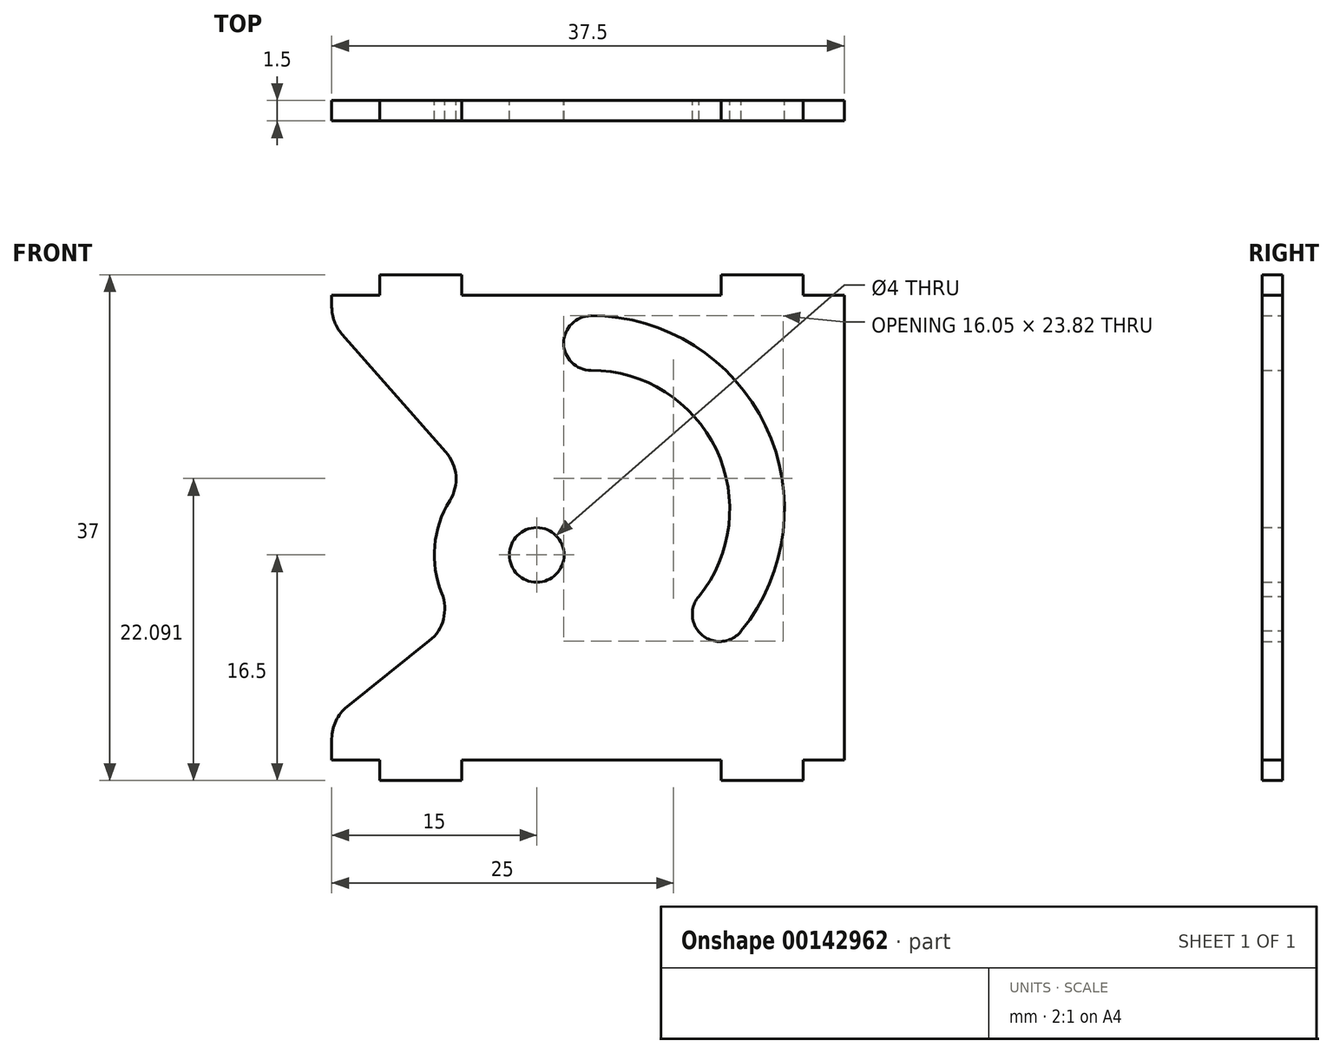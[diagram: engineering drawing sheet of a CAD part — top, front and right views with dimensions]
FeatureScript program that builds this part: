
annotation { "Feature Type Name" : "Feature", "Feature Type Description" : "" }
export const myFeature = defineFeature(function(context is Context, id is Id, definition is map)
    precondition{}
    {
        {
            var Q0;
            Q0=qCreatedBy(makeId("Front.planeOp"),FACE);
            var sketch = newSketch(context, id + "F0", { "sketchPlane" : qUnion([Q0])});
            skLineSegment(sketch, "E0.bottom", {"start": v(15, -19) * mm, "end": v(9, -19) * mm});
            skLineSegment(sketch, "E0.top", {"start": v(15, 18) * mm, "end": v(9, 18) * mm});
            skLineSegment(sketch, "E0.right", {"start": v(-19.5, -17.5) * mm, "end": v(-19.5, -15.94) * mm});
            skPoint(sketch, "E0.middle", {"position": v(0, 0) * mm});
            skLineSegment(sketch, "E1.0", {"start": v(18, -17.5) * mm, "end": v(15, -17.5) * mm});
            skLineSegment(sketch, "E2.0", {"start": v(18, 16.5) * mm, "end": v(15, 16.5) * mm});
            skLineSegment(sketch, "E3.0", {"start": v(-16, -19) * mm, "end": v(-16, -17.5) * mm});
            skLineSegment(sketch, "E4.0", {"start": v(15, -19) * mm, "end": v(15, -17.5) * mm});
            skLineSegment(sketch, "E5.0", {"start": v(-10, -19) * mm, "end": v(-10, -17.5) * mm});
            skLineSegment(sketch, "E6.0", {"start": v(9, -19) * mm, "end": v(9, -17.5) * mm});
            skLineSegment(sketch, "E7.trimOffspring", {"start": v(-10, -19) * mm, "end": v(-16, -19) * mm});
            skLineSegment(sketch, "E8.trimOffspring", {"start": v(-10, 18) * mm, "end": v(-16, 18) * mm});
            skLineSegment(sketch, "E9.trimOffspring", {"start": v(-10, 16.5) * mm, "end": v(-10, 18) * mm});
            skLineSegment(sketch, "E10.trimOffspring", {"start": v(9, 16.5) * mm, "end": v(9, 18) * mm});
            skLineSegment(sketch, "E11.trimOffspring", {"start": v(15, 16.5) * mm, "end": v(15, 18) * mm});
            skLineSegment(sketch, "E12.trimOffspring", {"start": v(-16, 16.5) * mm, "end": v(-16, 18) * mm});
            skCircle(sketch, "E13", {"center": v(-4.5, -2.5) * mm, "radius": 2 * mm});
            skArc(sketch, "E14", {"start": v(-10.86, 1.47) * mm, "mid": v(-11.97, -1.85) * mm, "end": v(-11.45, -5.32) * mm});
            skLineSegment(sketch, "E15", {"start": v(-18.75, 13.65) * mm, "end": v(-11.16, 5.05) * mm});
            skLineSegment(sketch, "E16", {"start": v(-18.37, -13.6) * mm, "end": v(-12.36, -8.79) * mm});
            skArc(sketch, "E17.filletArc", {"start": v(-10.86, 1.47) * mm, "mid": v(-10.42, 3.3) * mm, "end": v(-11.16, 5.05) * mm});
            skPoint(sketch, "E18.visualSharp", {"position": v(-10.36, -7.19) * mm});
            skArc(sketch, "E18.filletArc", {"start": v(-12.36, -8.79) * mm, "mid": v(-11.33, -7.2) * mm, "end": v(-11.45, -5.32) * mm});
            skLineSegment(sketch, "E19.trimOffspring", {"start": v(-19.5, 15.63) * mm, "end": v(-19.5, 16.5) * mm});
            skArc(sketch, "E20.filletArc", {"start": v(-19.5, 15.63) * mm, "mid": v(-19.3, 14.57) * mm, "end": v(-18.75, 13.65) * mm});
            skArc(sketch, "E21.filletArc", {"start": v(-18.37, -13.6) * mm, "mid": v(-19.2, -14.64) * mm, "end": v(-19.5, -15.94) * mm});
            skLineSegment(sketch, "E22", {"start": v(-4.5, -2.5) * mm, "end": v(-14.85, -2.5) * mm});
            skLineSegment(sketch, "E23.trimOffspring", {"start": v(-16, -17.5) * mm, "end": v(-19.5, -17.5) * mm});
            skLineSegment(sketch, "E24.trimOffspring", {"start": v(-16, 16.5) * mm, "end": v(-19.5, 16.5) * mm});
            skLineSegment(sketch, "E25.trimOffspring", {"start": v(9, 16.5) * mm, "end": v(-10, 16.5) * mm});
            skLineSegment(sketch, "E26", {"start": v(-10, -17.5) * mm, "end": v(9, -17.5) * mm});
            skArc(sketch, "E27.0", {"start": v(7.36, -5.54) * mm, "mid": v(8.63, 5.22) * mm, "end": v(-0.53, 11) * mm});
            skArc(sketch, "E28.0", {"start": v(10.47, -8.05) * mm, "mid": v(12.25, 6.94) * mm, "end": v(-0.53, 15) * mm});
            skArc(sketch, "E29", {"start": v(-0.53, 15) * mm, "mid": v(-2.53, 13) * mm, "end": v(-0.53, 11) * mm});
            skArc(sketch, "E30", {"start": v(7.36, -5.54) * mm, "mid": v(7.63, -8.39) * mm, "end": v(10.47, -8.05) * mm});
            skLineSegment(sketch, "E31.0", {"start": v(18, 16.5) * mm, "end": v(18, -17.5) * mm});
            skSolve(sketch);
        }
        {
            var Q0;
            Q0=makeQuery(id+"F0.imprint","IMPRINT",FACE,{"disambiguationData":[TD([[makeQuery(id+"F0.imprint","IMPRINT",EDGE,{"derivedFrom":sQuery(id+"F0.wireOp",EDGE,"E0.bottom")}),-1.0]])]});
            extrude(context, id + "F1", {"entities" : qUnion([Q0]), "depth" : 1.5 * mm});
        }
    });
